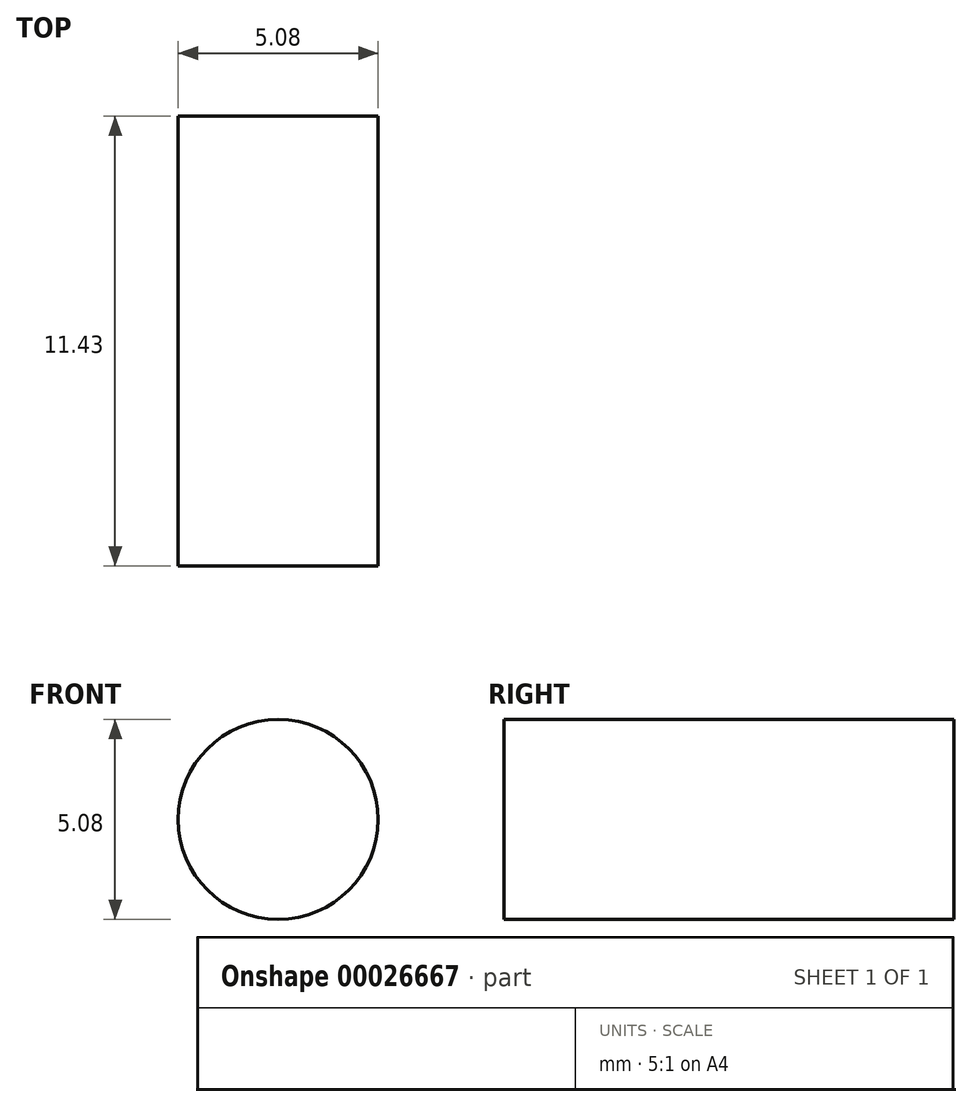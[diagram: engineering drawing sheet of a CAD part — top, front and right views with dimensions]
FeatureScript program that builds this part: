
annotation { "Feature Type Name" : "Feature", "Feature Type Description" : "" }
export const myFeature = defineFeature(function(context is Context, id is Id, definition is map)
    precondition{}
    {
        {
            var Q0;
            Q0=qCreatedBy(makeId("Front.planeOp"),FACE);
            var sketch = newSketch(context, id + "F0", { "sketchPlane" : qUnion([Q0])});
            skCircle(sketch, "E0", {"center": v(0, 0) * mm, "radius": 2.54 * mm});
            skSolve(sketch);
        }
        {
            var Q0;
            Q0=makeQuery(id+"F0.imprint","IMPRINT",FACE,{"disambiguationData":[TD([[makeQuery(id+"F0.imprint","IMPRINT",EDGE,{"derivedFrom":sQuery(id+"F0.wireOp",EDGE,"E0")}),1.0]])]});
            extrude(context, id + "F1", {"entities" : qUnion([Q0]), "depth" : 11.43 * mm});
        }
    });
